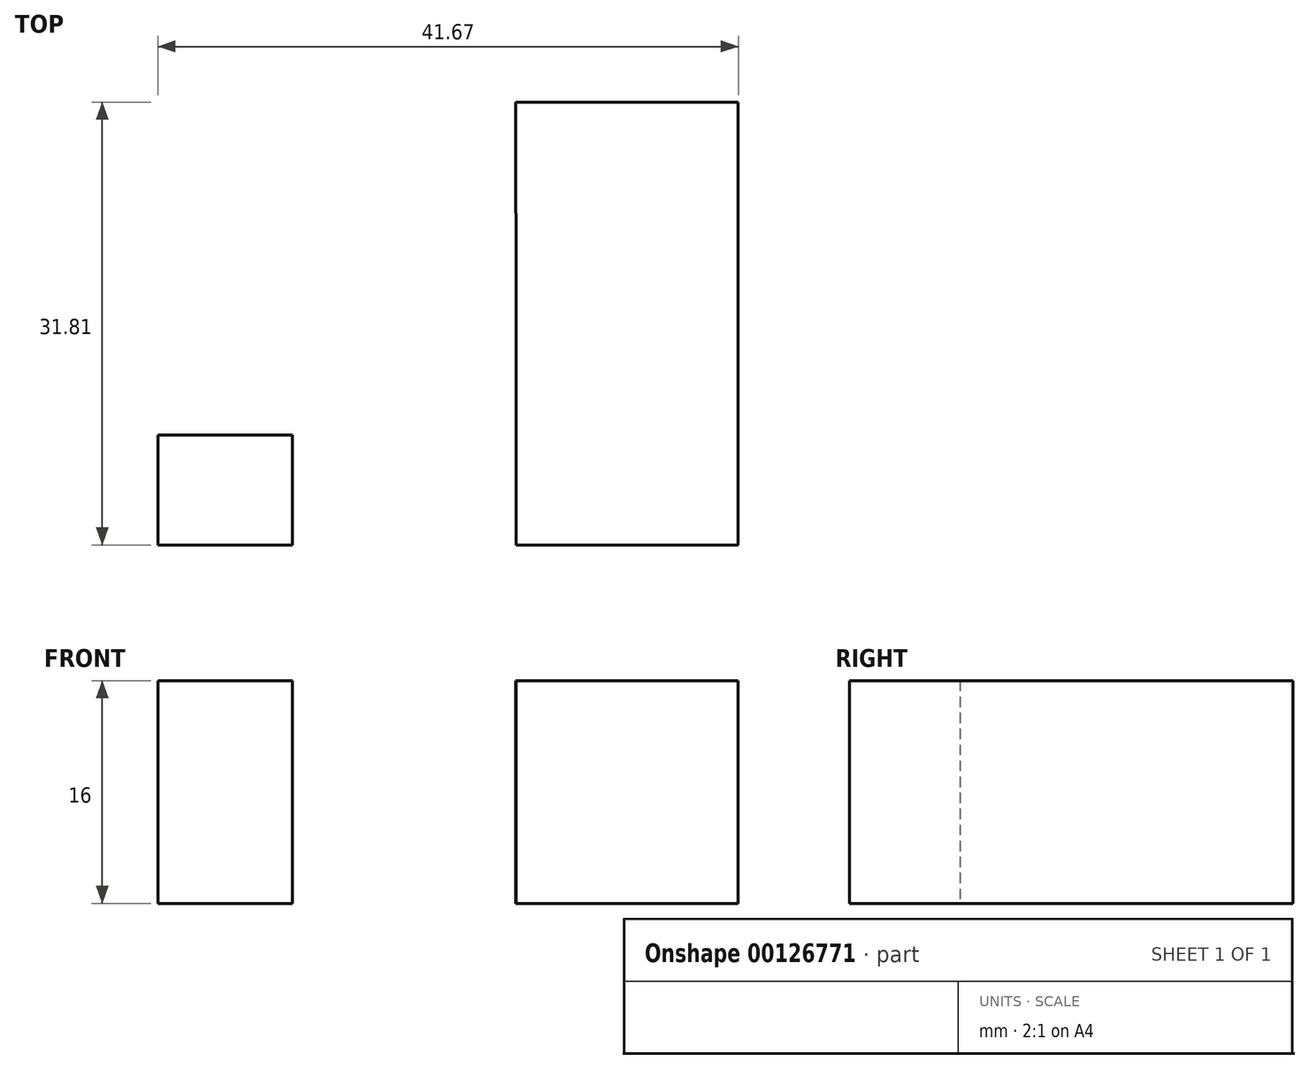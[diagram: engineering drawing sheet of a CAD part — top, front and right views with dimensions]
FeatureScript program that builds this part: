
annotation { "Feature Type Name" : "Feature", "Feature Type Description" : "" }
export const myFeature = defineFeature(function(context is Context, id is Id, definition is map)
    precondition{}
    {
        {
            var Q0;
            Q0=qCreatedBy(makeId("Top.planeOp"),FACE);
            var sketch = newSketch(context, id + "F0", { "sketchPlane" : qUnion([Q0])});
            skLineSegment(sketch, "E0.bottom", {"start": v(-36.53, 30.71) * mm, "end": v(-20.58, 30.71) * mm});
            skLineSegment(sketch, "E0.top", {"start": v(-36.53, 14.9) * mm, "end": v(-20.58, 14.9) * mm});
            skLineSegment(sketch, "E0.left", {"start": v(-36.53, 30.71) * mm, "end": v(-36.53, 14.9) * mm});
            skLineSegment(sketch, "E0.right", {"start": v(-20.58, 30.71) * mm, "end": v(-20.58, 14.9) * mm});
            skLineSegment(sketch, "E1", {"start": v(-52.6, 14.9) * mm, "end": v(-52.6, 22.8) * mm});
            skPoint(sketch, "E1.endSnap0", {"position": v(-20.58, 22.8) * mm});
            skLineSegment(sketch, "E2", {"start": v(-52.6, 22.8) * mm, "end": v(-62.25, 22.8) * mm});
            skLineSegment(sketch, "E3", {"start": v(-62.25, 22.8) * mm, "end": v(-62.25, 14.9) * mm});
            skLineSegment(sketch, "E4", {"start": v(-62.25, 14.9) * mm, "end": v(-52.6, 14.9) * mm});
            skLineSegment(sketch, "E5", {"start": v(-20.58, 46.71) * mm, "end": v(-36.58, 46.71) * mm});
            skLineSegment(sketch, "E6", {"start": v(-36.58, 46.71) * mm, "end": v(-36.53, 30.71) * mm});
            skLineSegment(sketch, "E7", {"start": v(-20.58, 46.71) * mm, "end": v(-20.58, 30.71) * mm});
            skLineSegment(sketch, "E8", {"start": v(-30.73, 46.71) * mm, "end": v(-30.73, 30.71) * mm});
            skSolve(sketch);
        }
        {
            var Q0;
            Q0 = qSketchRegion(id + "F0", true);
            extrude(context, id + "F1", {"entities" : qUnion([Q0]), "depth" : 16 * mm});
        }
        {
            var Q0;
            Q0=makeQuery(id+"F0.imprint","IMPRINT",FACE,{"disambiguationData":[TD([[makeQuery(id+"F0.imprint","IMPRINT",EDGE,{"derivedFrom":sQuery(id+"F0.wireOp",EDGE,"E0.bottom")}),-1.0]])]});
            extrude(context, id + "F2", {"entities" : qUnion([Q0]), "operationType" : NewBodyOperationType.ADD, "depth" : 16 * mm});
        }
        {
            var Q0;
            Q0=makeQuery(id+"F0.imprint","IMPRINT",FACE,{"disambiguationData":[TD([[makeQuery(id+"F0.imprint","IMPRINT",EDGE,{"derivedFrom":sQuery(id+"F0.wireOp",EDGE,"E1")}),1.0]])]});
            extrude(context, id + "F3", {"entities" : qUnion([Q0]), "operationType" : NewBodyOperationType.ADD, "depth" : 16 * mm});
        }
    });
